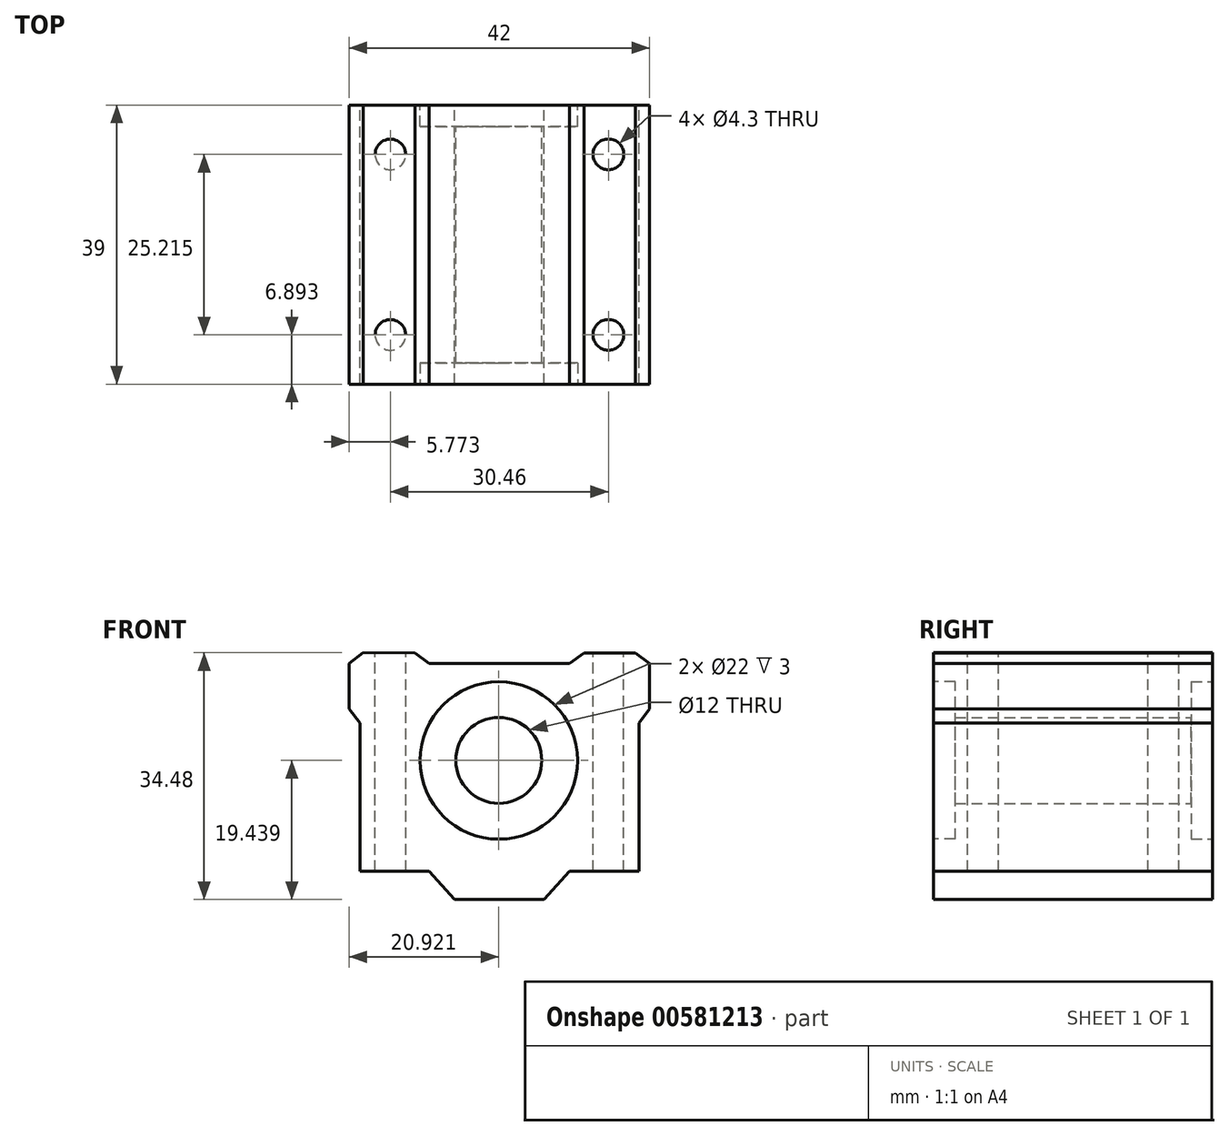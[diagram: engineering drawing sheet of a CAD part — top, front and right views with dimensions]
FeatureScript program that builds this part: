
annotation { "Feature Type Name" : "Feature", "Feature Type Description" : "" }
export const myFeature = defineFeature(function(context is Context, id is Id, definition is map)
    precondition{}
    {
        {
            var Q0;
            Q0=qCreatedBy(makeId("Front.planeOp"),FACE);
            var sketch = newSketch(context, id + "F0", { "sketchPlane" : qUnion([Q0])});
            skLineSegment(sketch, "E0", {"start": v(-25.05, 19.8) * mm, "end": v(-25.05, 13.43) * mm});
            skLineSegment(sketch, "E1", {"start": v(-25.05, 13.43) * mm, "end": v(-23.55, 11.46) * mm});
            skLineSegment(sketch, "E2", {"start": v(-23.55, 11.46) * mm, "end": v(-23.55, -9.21) * mm});
            skLineSegment(sketch, "E3", {"start": v(-23.55, -9.21) * mm, "end": v(-13.85, -9.21) * mm});
            skLineSegment(sketch, "E4", {"start": v(-13.85, -9.21) * mm, "end": v(-10.3, -13.19) * mm});
            skLineSegment(sketch, "E5", {"start": v(-10.3, -13.19) * mm, "end": v(2.2, -13.19) * mm});
            skLineSegment(sketch, "E6", {"start": v(2.2, -13.19) * mm, "end": v(5.75, -9.21) * mm});
            skLineSegment(sketch, "E7", {"start": v(5.75, -9.21) * mm, "end": v(15.45, -9.21) * mm});
            skLineSegment(sketch, "E8", {"start": v(15.45, -9.21) * mm, "end": v(15.45, 11.46) * mm});
            skLineSegment(sketch, "E9", {"start": v(15.45, 11.46) * mm, "end": v(16.95, 13.43) * mm});
            skLineSegment(sketch, "E10", {"start": v(16.95, 13.43) * mm, "end": v(16.95, 19.8) * mm});
            skLineSegment(sketch, "E11", {"start": v(14.95, 21.25) * mm, "end": v(7.76, 21.25) * mm});
            skLineSegment(sketch, "E12", {"start": v(7.76, 21.25) * mm, "end": v(5.75, 19.8) * mm});
            skLineSegment(sketch, "E13", {"start": v(5.75, 19.8) * mm, "end": v(-13.85, 19.8) * mm});
            skLineSegment(sketch, "E14", {"start": v(-13.85, 19.8) * mm, "end": v(-15.85, 21.25) * mm});
            skLineSegment(sketch, "E15", {"start": v(-15.85, 21.25) * mm, "end": v(-23.08, 21.3) * mm});
            skCircle(sketch, "E16", {"center": v(-4.13, 6.25) * mm, "radius": 6 * mm});
            skLineSegment(sketch, "E17", {"start": v(16.95, 19.8) * mm, "end": v(14.95, 21.25) * mm});
            skPoint(sketch, "E18.orphan", {"position": v(16.95, 21.25) * mm});
            skLineSegment(sketch, "E19", {"start": v(-25.05, 19.8) * mm, "end": v(-23.08, 21.3) * mm});
            skPoint(sketch, "E20.orphan", {"position": v(-25.05, 21.3) * mm});
            skSolve(sketch);
        }
        {
            var Q0;
            Q0 = qSketchRegion(id + "F0", true);
            extrude(context, id + "F1", {"entities" : qUnion([Q0]), "depth" : 39 * mm, "offsetDistance" : 25.4 * mm});
        }
        {
            var Q0;
            Q0=makeQuery(id+"F1.opExtrude","SWEPT_FACE",FACE,{"disambiguationData":[OSD([sQuery(id+"F0.wireOp",EDGE,"E13")])]});
            var sketch = newSketch(context, id + "F2", { "sketchPlane" : qUnion([Q0])});
            skPoint(sketch, "E21.endSnap0", {"position": v(5.75, -19.5) * mm});
            skCircle(sketch, "E22.MirrorC", {"center": v(-19.28, -6.9) * mm, "radius": 2.15 * mm});
            skPoint(sketch, "E23.startSnap0", {"position": v(-13.85, -19.5) * mm});
            skPoint(sketch, "E23.endSnap0", {"position": v(-4.05, -19.5) * mm});
            skCircle(sketch, "E24.MirrorC", {"center": v(-19.28, -32.1) * mm, "radius": 2.15 * mm});
            skCircle(sketch, "E25.MirrorC", {"center": v(11.18, -6.9) * mm, "radius": 2.15 * mm});
            skCircle(sketch, "E26.MirrorC", {"center": v(11.18, -32.1) * mm, "radius": 2.15 * mm});
            skSolve(sketch);
        }
        {
            var Q0;
            Q0 = qSketchRegion(id + "F2", true);
            extrude(context, id + "F3", {"entities" : qUnion([Q0]), "operationType" : NewBodyOperationType.REMOVE, "endBound" : BoundingType.SYMMETRIC, "oppositeDirection" : true, "depth" : 79.5 * mm, "offsetDistance" : 25.4 * mm});
        }
        {
            var Q0;
            Q0=makeQuery(id+"F1.opExtrude","CAP_FACE",FACE,{"disambiguationData":[OSD([sQuery(id+"F0.wireOp",EDGE,"E0"),sQuery(id+"F0.wireOp",EDGE,"E1"),sQuery(id+"F0.wireOp",EDGE,"E2"),sQuery(id+"F0.wireOp",EDGE,"E3"),sQuery(id+"F0.wireOp",EDGE,"E4"),sQuery(id+"F0.wireOp",EDGE,"E5"),sQuery(id+"F0.wireOp",EDGE,"E6"),sQuery(id+"F0.wireOp",EDGE,"E7"),sQuery(id+"F0.wireOp",EDGE,"E8"),sQuery(id+"F0.wireOp",EDGE,"E9"),sQuery(id+"F0.wireOp",EDGE,"E10"),sQuery(id+"F0.wireOp",EDGE,"E11"),sQuery(id+"F0.wireOp",EDGE,"E12"),sQuery(id+"F0.wireOp",EDGE,"E13"),sQuery(id+"F0.wireOp",EDGE,"E14"),sQuery(id+"F0.wireOp",EDGE,"E15"),sQuery(id+"F0.wireOp",EDGE,"E16"),sQuery(id+"F0.wireOp",EDGE,"E17"),sQuery(id+"F0.wireOp",EDGE,"E19")])],"isStart":true});
            var sketch = newSketch(context, id + "F4", { "sketchPlane" : qUnion([Q0])});
            skCircle(sketch, "E27", {"center": v(4.13, 6.25) * mm, "radius": 11 * mm});
            skSolve(sketch);
        }
        {
            var Q0;
            Q0=makeQuery(id+"F4.imprint","IMPRINT",FACE,{"disambiguationData":[TD([[makeQuery(id+"F4.imprint","IMPRINT",EDGE,{"derivedFrom":sQuery(id+"F4.wireOp",EDGE,"E27")}),1.0]])]});
            extrude(context, id + "F5", {"entities" : qUnion([Q0]), "operationType" : NewBodyOperationType.REMOVE, "oppositeDirection" : true, "depth" : 3 * mm, "offsetDistance" : 25.4 * mm});
        }
        {
            var Q0;
            Q0=makeQuery(id+"F1.opExtrude","CAP_FACE",FACE,{"disambiguationData":[OSD([sQuery(id+"F0.wireOp",EDGE,"E0"),sQuery(id+"F0.wireOp",EDGE,"E1"),sQuery(id+"F0.wireOp",EDGE,"E2"),sQuery(id+"F0.wireOp",EDGE,"E3"),sQuery(id+"F0.wireOp",EDGE,"E4"),sQuery(id+"F0.wireOp",EDGE,"E5"),sQuery(id+"F0.wireOp",EDGE,"E6"),sQuery(id+"F0.wireOp",EDGE,"E7"),sQuery(id+"F0.wireOp",EDGE,"E8"),sQuery(id+"F0.wireOp",EDGE,"E9"),sQuery(id+"F0.wireOp",EDGE,"E10"),sQuery(id+"F0.wireOp",EDGE,"E11"),sQuery(id+"F0.wireOp",EDGE,"E12"),sQuery(id+"F0.wireOp",EDGE,"E13"),sQuery(id+"F0.wireOp",EDGE,"E14"),sQuery(id+"F0.wireOp",EDGE,"E15"),sQuery(id+"F0.wireOp",EDGE,"E16"),sQuery(id+"F0.wireOp",EDGE,"E17"),sQuery(id+"F0.wireOp",EDGE,"E19")])],"isStart":false});
            var sketch = newSketch(context, id + "F6", { "sketchPlane" : qUnion([Q0])});
            skCircle(sketch, "E28", {"center": v(-4.13, 6.25) * mm, "radius": 11 * mm});
            skSolve(sketch);
        }
        {
            var Q0;
            Q0=makeQuery(id+"F6.imprint","IMPRINT",FACE,{"disambiguationData":[TD([[makeQuery(id+"F6.imprint","IMPRINT",EDGE,{"derivedFrom":sQuery(id+"F6.wireOp",EDGE,"E28")}),1.0]])]});
            extrude(context, id + "F7", {"entities" : qUnion([Q0]), "operationType" : NewBodyOperationType.REMOVE, "oppositeDirection" : true, "depth" : 3 * mm, "offsetDistance" : 25.4 * mm});
        }
    });
